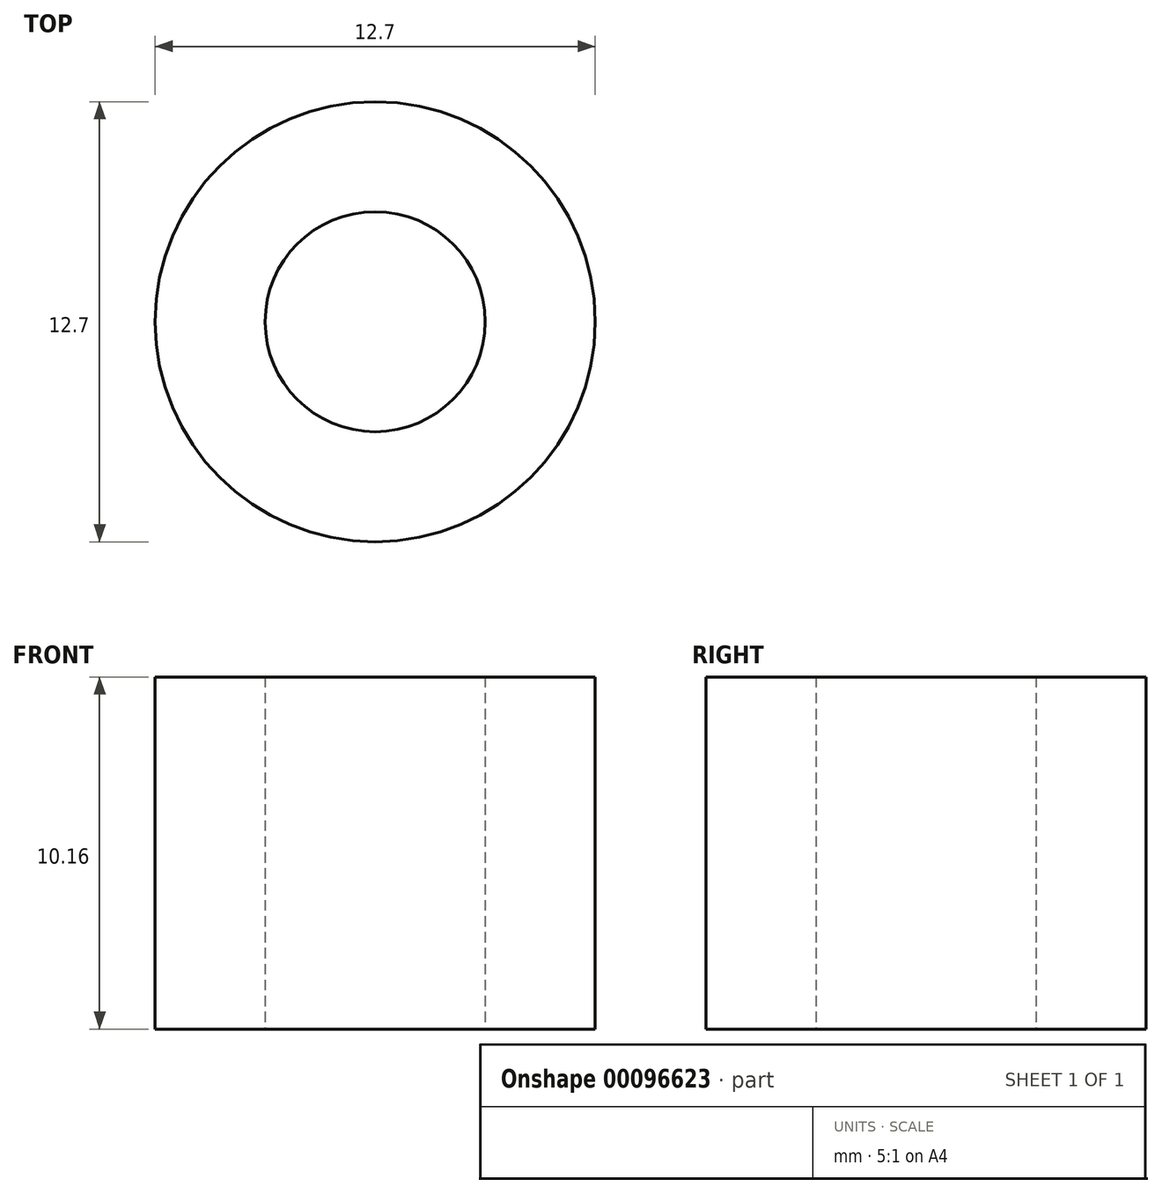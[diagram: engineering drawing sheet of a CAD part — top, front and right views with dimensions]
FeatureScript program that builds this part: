
annotation { "Feature Type Name" : "Feature", "Feature Type Description" : "" }
export const myFeature = defineFeature(function(context is Context, id is Id, definition is map)
    precondition{}
    {
        {
            var Q0;
            Q0=qCreatedBy(makeId("Top.planeOp"),FACE);
            var sketch = newSketch(context, id + "F0", { "sketchPlane" : qUnion([Q0])});
            skCircle(sketch, "E0", {"center": v(0, 0) * mm, "radius": 6.35 * mm});
            skCircle(sketch, "E1", {"center": v(0, 0) * mm, "radius": 3.18 * mm});
            skSolve(sketch);
        }
        {
            var Q0;
            Q0 = qSketchRegion(id + "F0", true);
            extrude(context, id + "F1", {"entities" : qUnion([Q0]), "depth" : 10.16 * mm});
        }
    });
